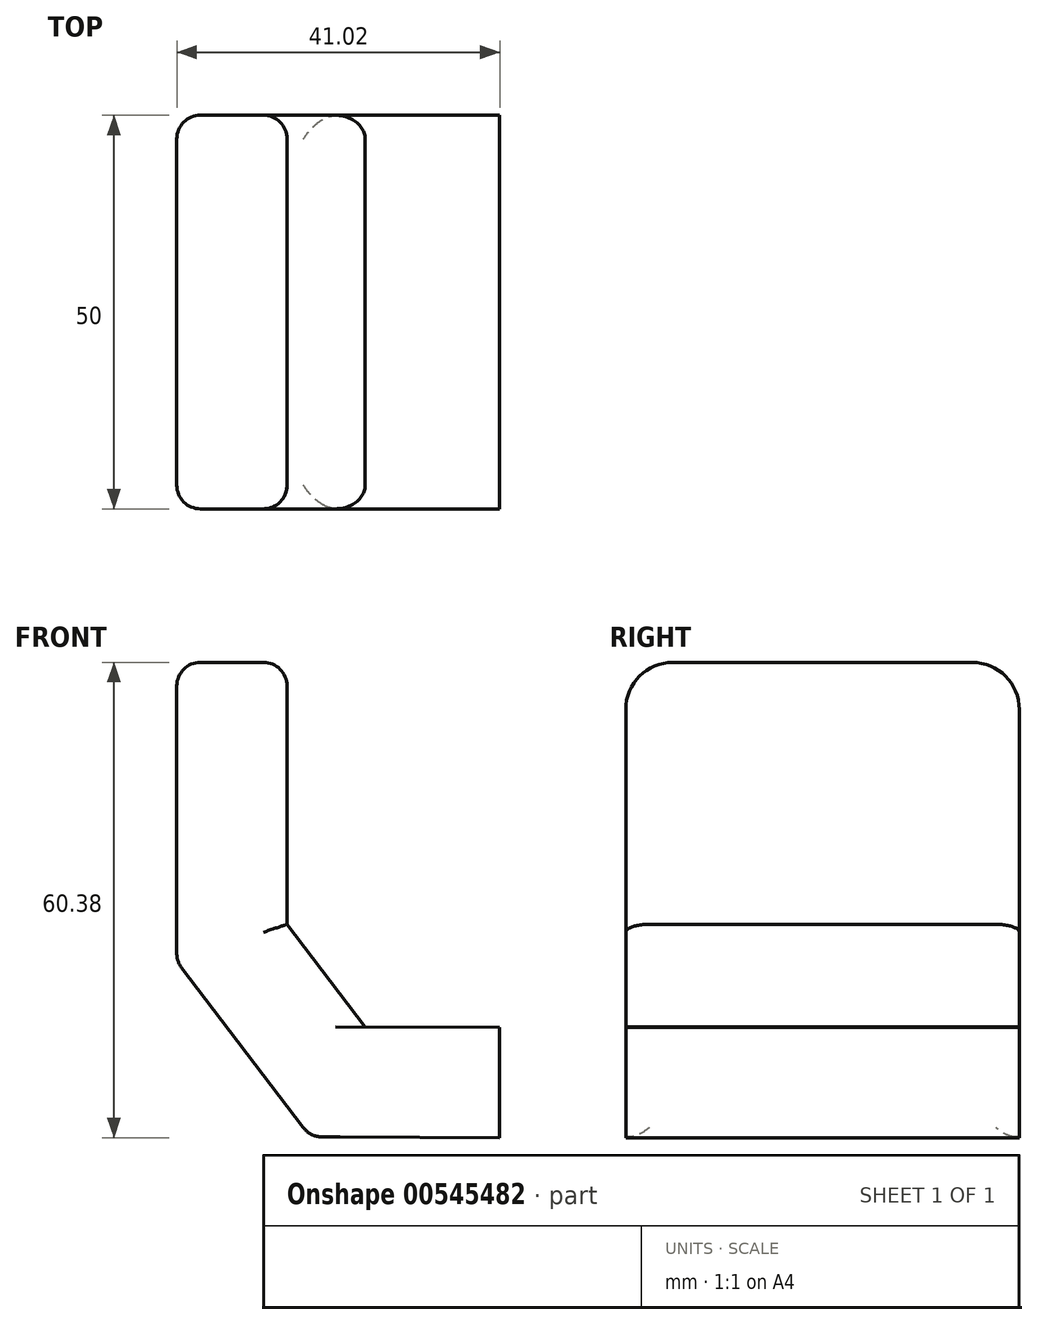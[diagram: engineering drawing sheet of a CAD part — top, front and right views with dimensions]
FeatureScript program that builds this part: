
annotation { "Feature Type Name" : "Feature", "Feature Type Description" : "" }
export const myFeature = defineFeature(function(context is Context, id is Id, definition is map)
    precondition{}
    {
        {
            var Q0;
            Q0=qCreatedBy(makeId("Front.planeOp"),FACE);
            var sketch = newSketch(context, id + "F0", { "sketchPlane" : qUnion([Q0])});
            skLineSegment(sketch, "E0", {"start": v(-63.76, 26.85) * mm, "end": v(-63.76, -11.15) * mm});
            skLineSegment(sketch, "E1", {"start": v(-63.76, -11.15) * mm, "end": v(-46.8, -33.43) * mm});
            skLineSegment(sketch, "E2", {"start": v(-46.8, -33.43) * mm, "end": v(-22.8, -33.53) * mm});
            skLineSegment(sketch, "E3.0", {"start": v(-39.84, -19.46) * mm, "end": v(-22.74, -19.53) * mm});
            skLineSegment(sketch, "E3.1", {"start": v(-49.76, -6.43) * mm, "end": v(-39.84, -19.46) * mm});
            skLineSegment(sketch, "E3.2", {"start": v(-49.76, 26.85) * mm, "end": v(-49.76, -6.43) * mm});
            skLineSegment(sketch, "E4", {"start": v(-63.76, 26.85) * mm, "end": v(-49.76, 26.85) * mm});
            skLineSegment(sketch, "E5", {"start": v(-22.74, -19.53) * mm, "end": v(-22.8, -33.53) * mm});
            skSolve(sketch);
        }
        {
            var Q0;
            Q0 = qSketchRegion(id + "F0", true);
            extrude(context, id + "F1", {"entities" : qUnion([Q0]), "depth" : 50 * mm, "offsetDistance" : 25 * mm});
        }
        {
            var Q0;
            Q0=makeQuery(id+"F1.opExtrude","CAP_EDGE",EDGE,{"disambiguationData":[OSD([sQuery(id+"F0.wireOp",EDGE,"E4")])],"isStart":false});
            var Q1;
            Q1=makeQuery(id+"F1.opExtrude","CAP_EDGE",EDGE,{"disambiguationData":[OSD([sQuery(id+"F0.wireOp",EDGE,"E4")])],"isStart":true});
            fillet(context, id + "F2", {"entities" : qUnion([Q0, Q1]), "radius" : 6 * mm, "tangentPropagation" : true, "allowEdgeOverflow" : false});
        }
        {
            var Q0;
            Q0=makeQuery(id+"F1.opExtrude","SWEPT_EDGE",EDGE,{"disambiguationData":[OSD([sQuery(id+"F0.wireOp",EDGE,"E0"),sQuery(id+"F0.wireOp",EDGE,"E1")])]});
            var Q1;
            Q1=makeQuery(id+"F1.opExtrude","CAP_EDGE",EDGE,{"disambiguationData":[OSD([sQuery(id+"F0.wireOp",EDGE,"E0")])],"isStart":false});
            var Q2;
            Q2=makeQuery(id+"F1.opExtrude","CAP_EDGE",EDGE,{"disambiguationData":[OSD([sQuery(id+"F0.wireOp",EDGE,"E1")])],"isStart":false});
            var Q3;
            Q3=makeQuery(id+"F1.opExtrude","CAP_EDGE",EDGE,{"disambiguationData":[OSD([sQuery(id+"F0.wireOp",EDGE,"E3.1")])],"isStart":false});
            var Q4;
            Q4=makeQuery(id+"F1.opExtrude","CAP_EDGE",EDGE,{"disambiguationData":[OSD([sQuery(id+"F0.wireOp",EDGE,"E3.2")])],"isStart":false});
            var Q5;
            Q5=makeQuery(id+"F1.opExtrude","SWEPT_EDGE",EDGE,{"disambiguationData":[OSD([sQuery(id+"F0.wireOp",EDGE,"E1"),sQuery(id+"F0.wireOp",EDGE,"E2")])]});
            var Q6;
            Q6=makeQuery(id+"F1.opExtrude","CAP_EDGE",EDGE,{"disambiguationData":[OSD([sQuery(id+"F0.wireOp",EDGE,"E1")])],"isStart":true});
            var Q7;
            Q7=makeQuery(id+"F1.opExtrude","CAP_EDGE",EDGE,{"disambiguationData":[OSD([sQuery(id+"F0.wireOp",EDGE,"E3.1")])],"isStart":true});
            fillet(context, id + "F3", {"entities" : qUnion([Q0, Q1, Q2, Q3, Q4, Q5, Q6, Q7]), "radius" : 3 * mm, "tangentPropagation" : true, "allowEdgeOverflow" : false});
        }
    });
